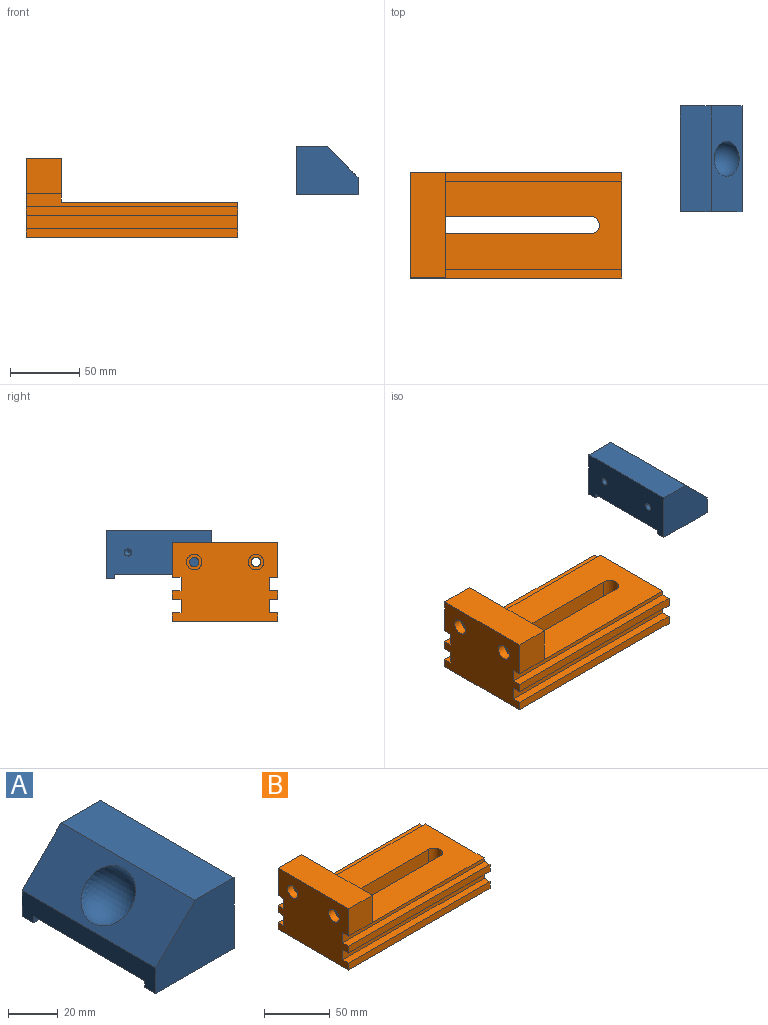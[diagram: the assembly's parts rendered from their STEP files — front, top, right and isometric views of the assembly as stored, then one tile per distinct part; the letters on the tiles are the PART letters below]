
ASSEMBLY  parts=2 mates=1
PART A: 16 faces, bbox 44.5x76.2x34.9 mm
  f0: plane 44.45x6.35mm, normal (0,0,-1), area 282.3mm2, adj f2,f5,f7,f10
  f1: plane 44.45x6.35mm, normal (0,0,-1), area 282.3mm2, adj f2,f5,f6,f8
  f2: plane 76.2x34.93mm, normal (1,0,0), area 2418.7mm2, adj f0,f1,f3,f6,f7,f8,f9,f10
  f3: plane 76.2x22.23mm, normal (0,0,1), area 1693.5mm2, adj f2,f4,f6,f7
  f4: plane 76.2x22.23mm, normal (-0.71,0,0.71), area 1888.3mm2, adj f3,f5,f6,f7,f15
  f5: plane 76.2x12.7mm, normal (-1,0,0), area 766.1mm2, adj f0,f1,f4,f6,f7,f8,f9,f10
  f6: plane 44.45x34.93mm, normal (0,-1,0), area 1305.4mm2, adj f1,f2,f3,f4,f5
  f7: plane 44.45x34.93mm, normal (0,1,0), area 1305.4mm2, adj f0,f2,f3,f4,f5
  f8: plane 44.45x3.18mm, normal (0,1,0), area 141.1mm2, adj f1,f2,f5,f9
  f9: plane 63.5x44.45mm, normal (0,0,-1), area 2822.6mm2, adj f2,f5,f8,f10
  f10: plane 44.45x3.18mm, normal (0,-1,0), area 141.1mm2, adj f0,f2,f5,f9
  f11: cylinder r=2.55mm len=12.7mm, axis (1,0,0), area 203.7mm2, adj f2,f12
  f12: cone r=0mm half-angle=59deg, axis (1,0,0), area 23.9mm2, adj f11
  f13: cylinder r=2.55mm len=12.7mm, axis (1,0,0), area 203.7mm2, adj f2,f14
  f14: cone r=0mm half-angle=59deg, axis (1,0,0), area 23.9mm2, adj f13
  f15: sphere r=12.7mm, area 1013.4mm2, adj f4
PART B: 45 faces, bbox 152.4x76.2x57.2 mm
  f0: plane 152.4x76.2mm, normal (0,0,-1), area 7816.9mm2, adj f2,f3,f21,f22,f29,f30,f31,f32
  f1: plane 127x63.5mm, normal (0,0,1), area 6670.5mm2, adj f2,f9,f15,f23,f25,f26,f27
  f2: plane 76.2x25.4mm, normal (1,0,0), area 1774.2mm2, adj f0,f1,f3,f4,f5,f6,f7,f8
  f3: plane 152.4x6.35mm, normal (0,1,0), area 967.7mm2, adj f0,f2,f4,f22
  f4: plane 152.4x6.35mm, normal (0,0,1), area 967.7mm2, adj f2,f3,f5,f22
  f5: plane 152.4x9.53mm, normal (0,1,0), area 1451.6mm2, adj f2,f4,f6,f22
  f6: plane 152.4x6.35mm, normal (0,0,-1), area 967.7mm2, adj f2,f5,f7,f22
  f7: plane 152.4x6.35mm, normal (0,1,0), area 967.7mm2, adj f2,f6,f8,f22
  f8: plane 152.4x6.35mm, normal (0,0,1), area 967.7mm2, adj f2,f7,f9,f22
  f9: plane 152.4x9.53mm, normal (0,1,0), area 645.2mm2, adj f1,f2,f8,f10,f22,f23
  f10: plane 25.4x6.35mm, normal (0,0,-1), area 161.3mm2, adj f9,f11,f22,f23
  f11: plane 25.4x25.4mm, normal (0,1,0), area 645.2mm2, adj f10,f12,f22,f23
  f12: plane 76.2x25.4mm, normal (0,0,1), area 1935.5mm2, adj f11,f13,f22,f23
  f13: plane 25.4x25.4mm, normal (0,-1,0), area 645.2mm2, adj f12,f14,f22,f23
  f14: plane 25.4x6.35mm, normal (0,0,-1), area 161.3mm2, adj f13,f15,f22,f23
  f15: plane 152.4x9.53mm, normal (0,-1,0), area 645.2mm2, adj f1,f2,f14,f16,f22,f23
  f16: plane 152.4x6.35mm, normal (0,0,1), area 967.7mm2, adj f2,f15,f17,f22
  f17: plane 152.4x6.35mm, normal (0,-1,0), area 967.7mm2, adj f2,f16,f18,f22
  f18: plane 152.4x6.35mm, normal (0,0,-1), area 967.7mm2, adj f2,f17,f19,f22
  f19: plane 152.4x9.53mm, normal (0,-1,0), area 1451.6mm2, adj f2,f18,f20,f22
  f20: plane 152.4x6.35mm, normal (0,0,1), area 967.7mm2, adj f2,f19,f21,f22
  f21: plane 152.4x6.35mm, normal (0,-1,0), area 967.7mm2, adj f0,f2,f20,f22
  f22: plane 76.2x57.15mm, normal (-1,0,0), area 3918.9mm2, adj f0,f3,f4,f5,f6,f7,f8,f9
  f23: plane 76.2x31.75mm, normal (1,0,0), area 2267mm2, adj f1,f9,f10,f11,f12,f13,f14,f15
  f24: plane 12.7x9.53mm, normal (0,0,-1), area 103.7mm2, adj f23,f25,f27,f28
  f25: plane 107.95x12.7mm, normal (0,-1,0), area 1371mm2, adj f1,f24,f26,f28,f34
  f26: cylinder r=6.35mm len=12.7mm, axis (0,0,-1), area 253.4mm2, adj f1,f25,f27,f34,f38
  f27: plane 107.95x12.7mm, normal (0,1,0), area 1371mm2, adj f1,f24,f26,f28,f38
  f28: cylinder r=6.35mm len=12.7mm, axis (0,0,-1), area 253.4mm2, adj f24,f25,f27,f34,f38
  f29: plane 19.05x12.7mm, normal (1,0,0), area 241.9mm2, adj f0,f30,f34,f37,f38
  f30: cylinder r=6.35mm len=12.7mm, axis (0,0,-1), area 126.7mm2, adj f0,f29,f31,f34
  f31: plane 107.95x12.7mm, normal (0,-1,0), area 1371mm2, adj f0,f30,f32,f34
  f32: cylinder r=6.35mm len=12.7mm, axis (0,0,-1), area 126.7mm2, adj f0,f31,f33,f34
  f33: plane 19.05x12.7mm, normal (-1,0,0), area 241.9mm2, adj f0,f32,f34,f35,f38
  f34: plane 120.65x15.88mm, normal (0,0,-1), area 1149.2mm2, adj f25,f26,f28,f29,f30,f31,f32,f33
  f35: cylinder r=6.35mm len=12.7mm, axis (0,0,-1), area 126.7mm2, adj f0,f33,f36,f38
  f36: plane 107.95x12.7mm, normal (0,1,0), area 1371mm2, adj f0,f35,f37,f38
  f37: cylinder r=6.35mm len=12.7mm, axis (0,0,-1), area 126.7mm2, adj f0,f29,f36,f38
  f38: plane 120.65x15.88mm, normal (0,0,-1), area 1149.2mm2, adj f26,f27,f28,f29,f33,f35,f36,f37
  f39: cylinder r=3.38mm len=19.05mm, axis (-1,0,0), area 404.4mm2, adj f23,f40
  f40: plane 11.11x11.11mm, normal (-1,0,0), area 61.1mm2, adj f39,f41
  f41: cylinder r=5.56mm len=11.11mm, axis (-1,0,0), area 221.7mm2, adj f22,f40
  f42: cylinder r=3.38mm len=19.05mm, axis (-1,0,0), area 404.4mm2, adj f23,f43
  f43: plane 11.11x11.11mm, normal (-1,0,0), area 61.1mm2, adj f42,f44
  f44: cylinder r=5.56mm len=11.11mm, axis (-1,0,0), area 221.7mm2, adj f22,f43
PLACE A rot(axis=(0,0,1),180deg) t=(224.76,57.88,21.77)mm
PLACE B t=(-14.42,10.17,-8.96)mm fixed
MATE parallel A.f13 <-> B.f23  axis (-1,0,0) through (180.31,35.66,40.82)mm
